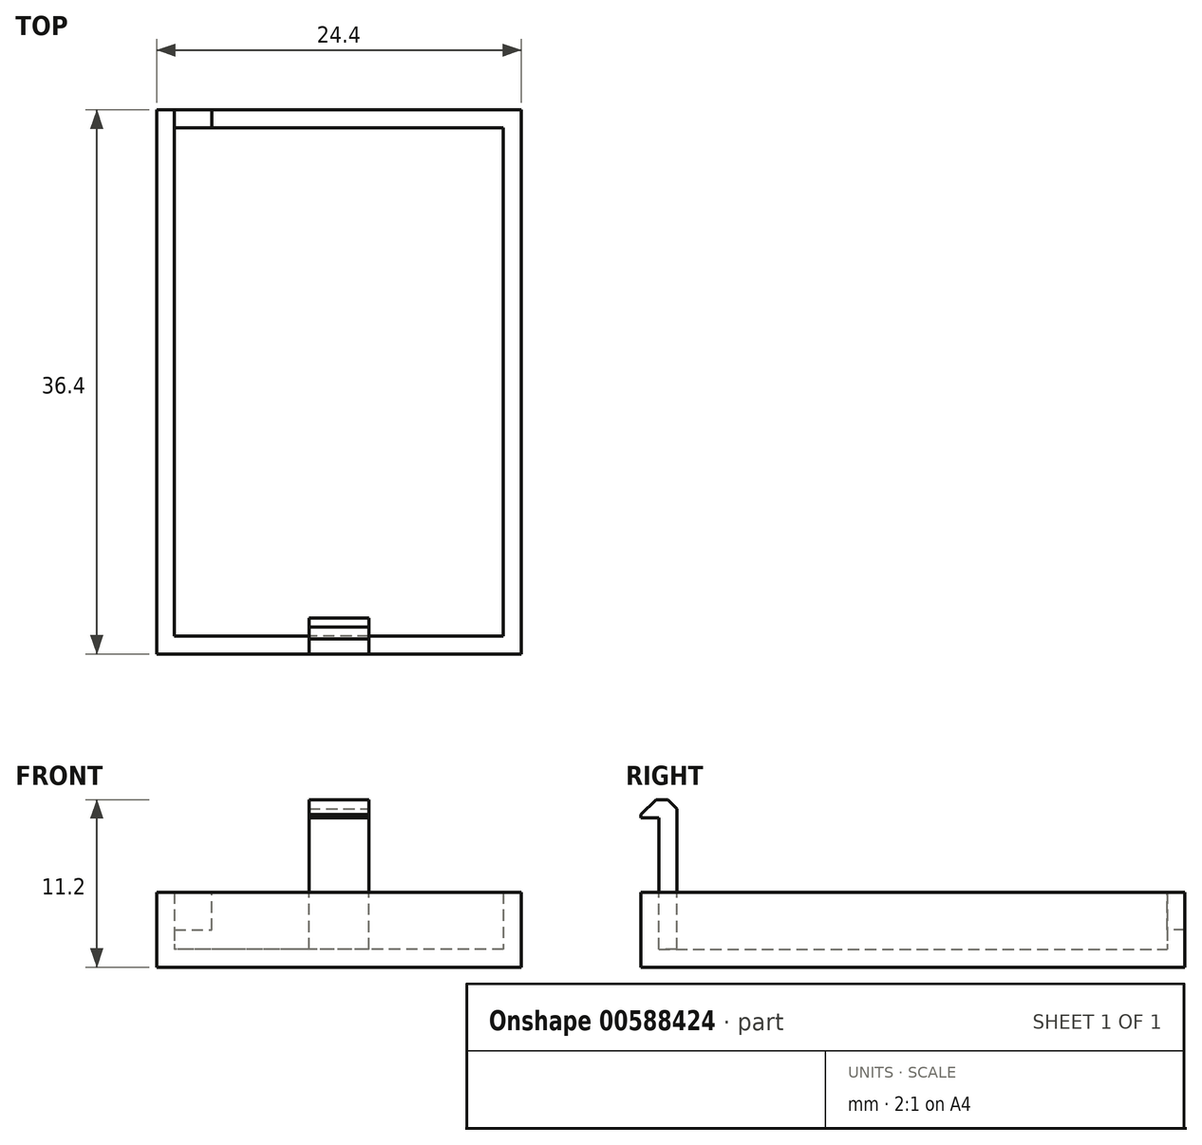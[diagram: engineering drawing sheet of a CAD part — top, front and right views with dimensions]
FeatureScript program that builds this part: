
annotation { "Feature Type Name" : "Feature", "Feature Type Description" : "" }
export const myFeature = defineFeature(function(context is Context, id is Id, definition is map)
    precondition{}
    {
        {
            var Q0;
            Q0=qCreatedBy(makeId("Top.planeOp"),FACE);
            var sketch = newSketch(context, id + "F0", { "sketchPlane" : qUnion([Q0])});
            skLineSegment(sketch, "E0.bottom", {"start": v(11, -17) * mm, "end": v(-11, -17) * mm});
            skLineSegment(sketch, "E0.top", {"start": v(11, 17) * mm, "end": v(-11, 17) * mm});
            skLineSegment(sketch, "E0.left", {"start": v(11, -17) * mm, "end": v(11, 17) * mm});
            skLineSegment(sketch, "E0.right", {"start": v(-11, -17) * mm, "end": v(-11, 17) * mm});
            skPoint(sketch, "E0.middle", {"position": v(0, 0) * mm});
            skLineSegment(sketch, "E1.0", {"start": v(12.2, 18.2) * mm, "end": v(-12.2, 18.2) * mm});
            skLineSegment(sketch, "E1.1", {"start": v(12.2, -18.2) * mm, "end": v(12.2, 18.2) * mm});
            skLineSegment(sketch, "E1.2", {"start": v(12.2, -18.2) * mm, "end": v(-12.2, -18.2) * mm});
            skLineSegment(sketch, "E1.3", {"start": v(-12.2, -18.2) * mm, "end": v(-12.2, 18.2) * mm});
            skSolve(sketch);
        }
        {
            var Q0;
            Q0=makeQuery(id+"F0.imprint","IMPRINT",FACE,{"disambiguationData":[TD([[makeQuery(id+"F0.imprint","IMPRINT",EDGE,{"derivedFrom":sQuery(id+"F0.wireOp",EDGE,"E0.bottom")}),-1.0]])]});
            extrude(context, id + "F1", {"entities" : qUnion([Q0]), "depth" : 1.2 * mm, "offsetDistance" : 25 * mm});
        }
        {
            var Q0;
            Q0 = qSketchRegion(id + "F0", true);
            extrude(context, id + "F2", {"entities" : qUnion([Q0]), "operationType" : NewBodyOperationType.ADD, "depth" : 5 * mm, "offsetDistance" : 25 * mm});
        }
        {
            var Q0;
            Q0=makeQuery(id+"F2.opExtrude","SWEPT_FACE",FACE,{"disambiguationData":[OSD([sQuery(id+"F0.wireOp",EDGE,"E0.bottom")])]});
            var sketch = newSketch(context, id + "F3", { "sketchPlane" : qUnion([Q0])});
            skLineSegment(sketch, "E2.bottom", {"start": v(-2, 1.2) * mm, "end": v(2, 1.2) * mm});
            skLineSegment(sketch, "E2.top", {"start": v(-2, 11.2) * mm, "end": v(2, 11.2) * mm});
            skLineSegment(sketch, "E2.left", {"start": v(-2, 1.2) * mm, "end": v(-2, 11.2) * mm});
            skLineSegment(sketch, "E2.right", {"start": v(2, 1.2) * mm, "end": v(2, 11.2) * mm});
            skSolve(sketch);
        }
        {
            var Q0;
            {var subQ0=sQuery(id+"F3.wireOp",EDGE,"E2.top");Q0=makeQuery(id+"F3.imprint","IMPRINT",FACE,{"disambiguationData":[TD([[makeQuery(id+"F3.imprint","IMPRINT",EDGE,{"derivedFrom":subQ0}),-1.0]])]});}
            var Q1;
            {var subQ0=sQuery(id+"F3.wireOp",EDGE,"E2.bottom");Q1=makeQuery(id+"F3.imprint","IMPRINT",FACE,{"disambiguationData":[TD([[makeQuery(id+"F3.imprint","IMPRINT",EDGE,{"derivedFrom":subQ0}),1.0]])]});}
            extrude(context, id + "F4", {"entities" : qUnion([Q0, Q1]), "operationType" : NewBodyOperationType.ADD, "depth" : 1.2 * mm, "offsetDistance" : 25 * mm});
        }
        {
            var Q0;
            Q0=makeQuery(id+"F4.opExtrude","CAP_EDGE",EDGE,{"disambiguationData":[OSD([sQuery(id+"F3.wireOp",EDGE,"E2.top")])],"isStart":false});
            chamfer(context, id + "F5", {"entities" : qUnion([Q0]), "width" : .6 * mm, "tangentPropagation" : true});
        }
        {
            var Q0;
            Q0=makeQuery(id+"F4.opExtrude","CAP_FACE",FACE,{"disambiguationData":[OSD([sQuery(id+"F3.wireOp",EDGE,"E2.bottom"),sQuery(id+"F3.wireOp",EDGE,"E2.top"),sQuery(id+"F3.wireOp",EDGE,"E2.left"),sQuery(id+"F3.wireOp",EDGE,"E2.right")])],"isStart":true});
            var sketch = newSketch(context, id + "F6", { "sketchPlane" : qUnion([Q0])});
            skLineSegment(sketch, "E3.bottom", {"start": v(-2, 11.2) * mm, "end": v(2, 11.2) * mm});
            skLineSegment(sketch, "E3.top", {"start": v(-2, 10) * mm, "end": v(2, 10) * mm});
            skLineSegment(sketch, "E3.left", {"start": v(-2, 11.2) * mm, "end": v(-2, 10) * mm});
            skLineSegment(sketch, "E3.right", {"start": v(2, 11.2) * mm, "end": v(2, 10) * mm});
            skSolve(sketch);
        }
        {
            var Q0;
            Q0=makeQuery(id+"F6.imprint","IMPRINT",FACE,{"disambiguationData":[TD([[makeQuery(id+"F6.imprint","IMPRINT",EDGE,{"derivedFrom":sQuery(id+"F6.wireOp",EDGE,"E3.bottom")}),1.0]])]});
            extrude(context, id + "F7", {"entities" : qUnion([Q0]), "operationType" : NewBodyOperationType.ADD, "depth" : 1.2 * mm, "offsetDistance" : 25 * mm});
        }
        {
            var Q0;
            Q0=makeQuery(id+"F7.opExtrude","CAP_EDGE",EDGE,{"disambiguationData":[OSD([sQuery(id+"F6.wireOp",EDGE,"E3.bottom")])],"isStart":false});
            chamfer(context, id + "F8", {"entities" : qUnion([Q0]), "width" : 1 * mm, "tangentPropagation" : true});
        }
        {
            var Q0;
            {var subQ1=sQuery(id+"F0.wireOp",EDGE,"E0.right");var subQ3=sQuery(id+"F0.wireOp",EDGE,"E0.top");Q0=makeQuery(id+"F4oSr1zhP9W6UVE_1.1.F4.boolean.opBoolean","SPLIT",FACE,{"disambiguationData":[TD([makeQuery(id+"F2.opExtrude","SWEPT_FACE",FACE,{"disambiguationData":[OSD([subQ1])]})])],"derivedFrom":makeQuery(id+"F2.opExtrude","SWEPT_FACE",FACE,{"disambiguationData":[OSD([subQ3])]})});}
            var sketch = newSketch(context, id + "F9", { "sketchPlane" : qUnion([Q0])});
            skLineSegment(sketch, "E4.bottom", {"start": v(-11, 2.5) * mm, "end": v(-8.5, 2.5) * mm});
            skLineSegment(sketch, "E4.top", {"start": v(-11, 5) * mm, "end": v(-8.5, 5) * mm});
            skLineSegment(sketch, "E4.left", {"start": v(-11, 2.5) * mm, "end": v(-11, 5) * mm});
            skLineSegment(sketch, "E4.right", {"start": v(-8.5, 2.5) * mm, "end": v(-8.5, 5) * mm});
            skSolve(sketch);
        }
        {
            var Q0;
            Q0=makeQuery(id+"F9.imprint","IMPRINT",FACE,{"disambiguationData":[TD([[makeQuery(id+"F9.imprint","IMPRINT",EDGE,{"derivedFrom":sQuery(id+"F9.wireOp",EDGE,"E4.bottom")}),1.0]])]});
            extrude(context, id + "F10", {"entities" : qUnion([Q0]), "operationType" : NewBodyOperationType.REMOVE, "oppositeDirection" : true, "depth" : 25 * mm, "offsetDistance" : 25 * mm});
        }
    });
